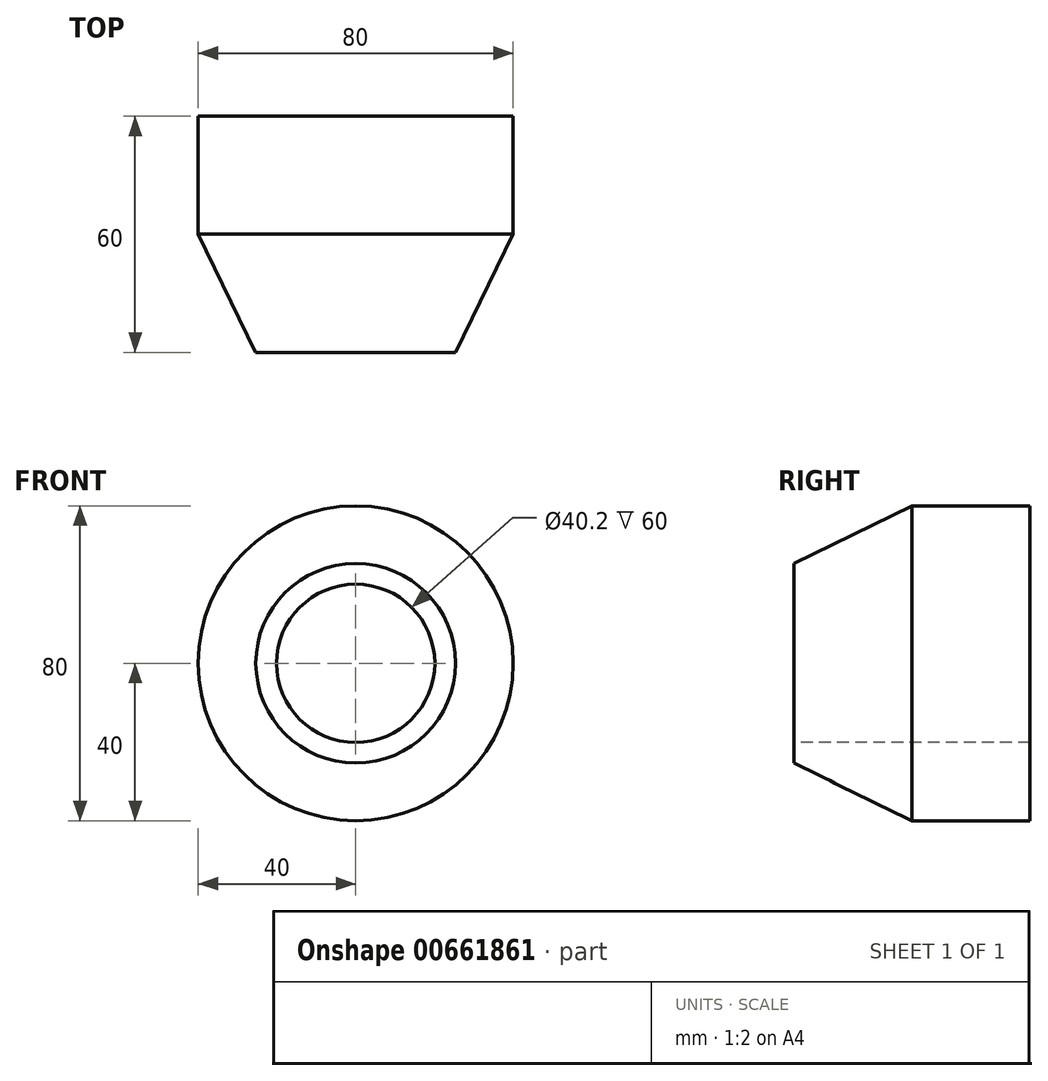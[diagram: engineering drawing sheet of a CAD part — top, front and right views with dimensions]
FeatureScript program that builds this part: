
annotation { "Feature Type Name" : "Feature", "Feature Type Description" : "" }
export const myFeature = defineFeature(function(context is Context, id is Id, definition is map)
    precondition{}
    {
        {
            var Q0;
            Q0=qCreatedBy(makeId("Front.planeOp"),FACE);
            var sketch = newSketch(context, id + "F0", { "sketchPlane" : qUnion([Q0])});
            skCircle(sketch, "E0", {"center": v(0, 0) * mm, "radius": 50 * mm, "construction": true});
            skCircle(sketch, "E1", {"center": v(0, 0) * mm, "radius": 40 * mm});
            skSolve(sketch);
        }
        {
            var Q0;
            Q0=makeQuery(id+"F0.imprint","IMPRINT",FACE,{"disambiguationData":[TD([[makeQuery(id+"F0.imprint","IMPRINT",EDGE,{"derivedFrom":sQuery(id+"F0.wireOp",EDGE,"E1")}),1.0]])]});
            extrude(context, id + "F1", {"entities" : qUnion([Q0]), "depth" : 30 * mm, "offsetDistance" : 25 * mm});
        }
        {
            var Q0;
            Q0=makeQuery(id+"F1.opExtrude","CAP_FACE",FACE,{"disambiguationData":[OSD([sQuery(id+"F0.wireOp",EDGE,"E1")])],"isStart":false});
            extrude(context, id + "F2", {"entities" : qUnion([Q0]), "operationType" : NewBodyOperationType.ADD, "depth" : 30 * mm, "offsetDistance" : 25 * mm, "hasDraft" : true, "draftAngle" : 26 * degree, "draftPullDirection" : true});
        }
        {
            var Q0;
            Q0=makeQuery(id+"F2.opExtrude","CAP_FACE",FACE,{"disambiguationData":[OSD([sQuery(id+"F0.wireOp",EDGE,"E1")])],"isStart":false});
            var sketch = newSketch(context, id + "F3", { "sketchPlane" : qUnion([Q0])});
            skCircle(sketch, "E2", {"center": v(0, 0) * mm, "radius": 20.1 * mm});
            skSolve(sketch);
        }
        {
            var Q0;
            Q0=makeQuery(id+"F3.imprint","IMPRINT",FACE,{"disambiguationData":[TD([[makeQuery(id+"F3.imprint","IMPRINT",EDGE,{"derivedFrom":sQuery(id+"F3.wireOp",EDGE,"E2")}),1.0]])]});
            extrude(context, id + "F4", {"entities" : qUnion([Q0]), "operationType" : NewBodyOperationType.REMOVE, "endBound" : BoundingType.THROUGH_ALL, "oppositeDirection" : true, "depth" : 25 * mm, "offsetDistance" : 25 * mm});
        }
    });
